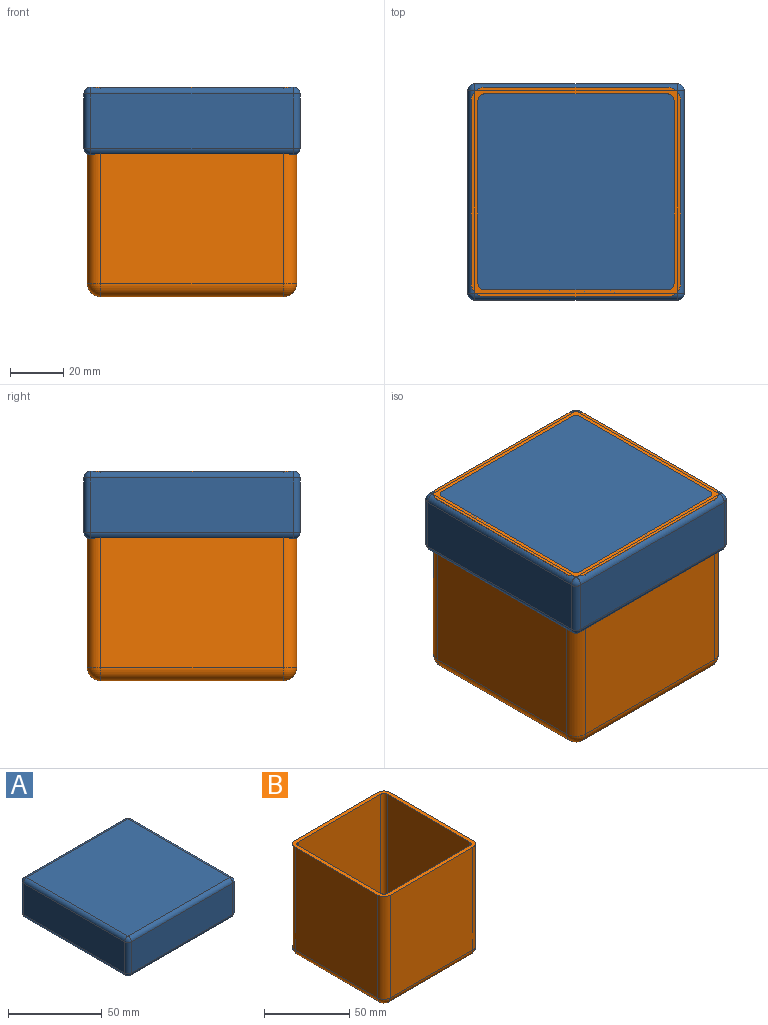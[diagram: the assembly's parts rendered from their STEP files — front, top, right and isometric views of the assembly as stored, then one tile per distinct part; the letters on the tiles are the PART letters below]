
ASSEMBLY  parts=2 mates=1
PART A: 30 faces, bbox 81.3x81.3x25.4 mm
  f0: plane 76.2x20.32mm, normal (0,1,0), area 1548.4mm2, adj f18,f23,f26,f29
  f1: plane 76.2x20.32mm, normal (-1,0,0), area 1548.4mm2, adj f15,f24,f25,f29
  f2: plane 76.2x20.32mm, normal (0,-1,0), area 1548.4mm2, adj f10,f14,f15,f16
  f3: plane 76.2x20.32mm, normal (1,0,0), area 1548.4mm2, adj f10,f13,f17,f18
  f4: plane 76.2x76.2mm, normal (0,0,1), area 5806.4mm2, adj f13,f14,f23,f24
  f5: plane 76.2x22.86mm, normal (0,-1,0), area 1741.9mm2, adj f6,f8,f9,f26
  f6: plane 76.2x22.86mm, normal (1,0,0), area 1741.9mm2, adj f5,f7,f9,f25
  f7: plane 76.2x22.86mm, normal (0,1,0), area 1741.9mm2, adj f6,f8,f9,f16
  f8: plane 76.2x22.86mm, normal (-1,0,0), area 1741.9mm2, adj f5,f7,f9,f17
  f9: plane 76.2x76.2mm, normal (0,0,-1), area 5806.4mm2, adj f5,f6,f7,f8
  f10: cylinder r=2.54mm len=20.32mm, axis (0,0,1), area 81.1mm2, adj f2,f3,f11,f12
  f11: sphere r=2.54mm, area 10.1mm2, adj f10,f13,f14
  f12: sphere r=2.54mm, area 10.1mm2, adj f10,f16,f17
  f13: cylinder r=2.54mm len=76.2mm, axis (0,-1,0), area 304mm2, adj f3,f4,f11,f19
  f14: cylinder r=2.54mm len=76.2mm, axis (-1,0,0), area 304mm2, adj f2,f4,f11,f20
  f15: cylinder r=2.54mm len=20.32mm, axis (0,0,-1), area 81.1mm2, adj f1,f2,f20,f21
  f16: cylinder r=2.54mm len=76.2mm, axis (1,0,0), area 304mm2, adj f2,f7,f12,f21
  f17: cylinder r=2.54mm len=76.2mm, axis (0,1,0), area 304mm2, adj f3,f8,f12,f22
  f18: cylinder r=2.54mm len=20.32mm, axis (0,0,-1), area 81.1mm2, adj f0,f3,f19,f22
  f19: sphere r=2.54mm, area 10.1mm2, adj f13,f18,f23
  f20: sphere r=2.54mm, area 10.1mm2, adj f14,f15,f24
  f21: sphere r=2.54mm, area 10.1mm2, adj f15,f16,f25
  f22: sphere r=2.54mm, area 10.1mm2, adj f17,f18,f26
  f23: cylinder r=2.54mm len=76.2mm, axis (1,0,0), area 304mm2, adj f0,f4,f19,f27
  f24: cylinder r=2.54mm len=76.2mm, axis (0,1,0), area 304mm2, adj f1,f4,f20,f27
  f25: cylinder r=2.54mm len=76.2mm, axis (0,-1,0), area 304mm2, adj f1,f6,f21,f28
  f26: cylinder r=2.54mm len=76.2mm, axis (-1,0,0), area 304mm2, adj f0,f5,f22,f28
  f27: sphere r=2.54mm, area 10.1mm2, adj f23,f24,f29
  f28: sphere r=2.54mm, area 10.1mm2, adj f25,f26,f29
  f29: cylinder r=2.54mm len=20.32mm, axis (0,0,1), area 81.1mm2, adj f0,f1,f27,f28
PART B: 35 faces, bbox 78.7x78.7x78.7 mm
  f0: plane 78.74x78.74mm, normal (0,0,1), area 757.6mm2, adj f1,f2,f3,f4,f6,f8,f11,f17
  f1: plane 73.66x68.58mm, normal (0,1,0), area 5051.6mm2, adj f0,f11,f15,f17
  f2: plane 73.66x68.58mm, normal (-1,0,0), area 5051.6mm2, adj f0,f8,f14,f17
  f3: plane 73.66x68.58mm, normal (0,-1,0), area 5051.6mm2, adj f0,f6,f8,f9
  f4: plane 73.66x68.58mm, normal (1,0,0), area 5051.6mm2, adj f0,f6,f10,f11
  f5: plane 68.58x68.58mm, normal (0,0,-1), area 4703.2mm2, adj f9,f10,f14,f15
  f6: cylinder r=5.08mm len=73.66mm, axis (0,0,1), area 587.8mm2, adj f0,f3,f4,f7
  f7: sphere r=5.08mm, area 40.5mm2, adj f6,f9,f10
  f8: cylinder r=5.08mm len=73.66mm, axis (0,0,-1), area 587.8mm2, adj f0,f2,f3,f12
  f9: cylinder r=5.08mm len=68.58mm, axis (1,0,0), area 547.2mm2, adj f3,f5,f7,f12
  f10: cylinder r=5.08mm len=68.58mm, axis (0,1,0), area 547.2mm2, adj f4,f5,f7,f13
  f11: cylinder r=5.08mm len=73.66mm, axis (0,0,-1), area 587.8mm2, adj f0,f1,f4,f13
  f12: sphere r=5.08mm, area 40.5mm2, adj f8,f9,f14
  f13: sphere r=5.08mm, area 40.5mm2, adj f10,f11,f15
  f14: cylinder r=5.08mm len=68.58mm, axis (0,-1,0), area 547.2mm2, adj f2,f5,f12,f16
  f15: cylinder r=5.08mm len=68.58mm, axis (-1,0,0), area 547.2mm2, adj f1,f5,f13,f16
  f16: sphere r=5.08mm, area 40.5mm2, adj f14,f15,f17
  f17: cylinder r=5.08mm len=73.66mm, axis (0,0,1), area 587.8mm2, adj f0,f1,f2,f16
  f18: plane 73.66x68.58mm, normal (0,-1,0), area 5051.6mm2, adj f0,f28,f32,f34
  f19: plane 73.66x68.58mm, normal (1,0,0), area 5051.6mm2, adj f0,f25,f31,f34
  f20: plane 73.66x68.58mm, normal (0,1,0), area 5051.6mm2, adj f0,f23,f25,f26
  f21: plane 73.66x68.58mm, normal (-1,0,0), area 5051.6mm2, adj f0,f23,f27,f28
  f22: plane 68.58x68.58mm, normal (0,0,1), area 4703.2mm2, adj f26,f27,f31,f32
  f23: cylinder r=2.54mm len=73.66mm, axis (0,0,1), area 293.9mm2, adj f0,f20,f21,f24
  f24: sphere r=2.54mm, area 10.1mm2, adj f23,f26,f27
  f25: cylinder r=2.54mm len=73.66mm, axis (0,0,-1), area 293.9mm2, adj f0,f19,f20,f29
  f26: cylinder r=2.54mm len=68.58mm, axis (1,0,0), area 273.6mm2, adj f20,f22,f24,f29
  f27: cylinder r=2.54mm len=68.58mm, axis (0,1,0), area 273.6mm2, adj f21,f22,f24,f30
  f28: cylinder r=2.54mm len=73.66mm, axis (0,0,-1), area 293.9mm2, adj f0,f18,f21,f30
  f29: sphere r=2.54mm, area 10.1mm2, adj f25,f26,f31
  f30: sphere r=2.54mm, area 10.1mm2, adj f27,f28,f32
  f31: cylinder r=2.54mm len=68.58mm, axis (0,-1,0), area 273.6mm2, adj f19,f22,f29,f33
  f32: cylinder r=2.54mm len=68.58mm, axis (-1,0,0), area 273.6mm2, adj f18,f22,f30,f33
  f33: sphere r=2.54mm, area 10.1mm2, adj f31,f32,f34
  f34: cylinder r=2.54mm len=73.66mm, axis (0,0,1), area 293.9mm2, adj f0,f18,f19,f33
PLACE A rot(axis=(0,0,1),180deg) t=(-3.16,8.21,26.12)mm
PLACE B t=(-37.56,21.14,-27.22)mm fixed
MATE slider A.f4 <-> B.f22  axis (0,0,1) through (-6.1,4.58,51.52)mm
